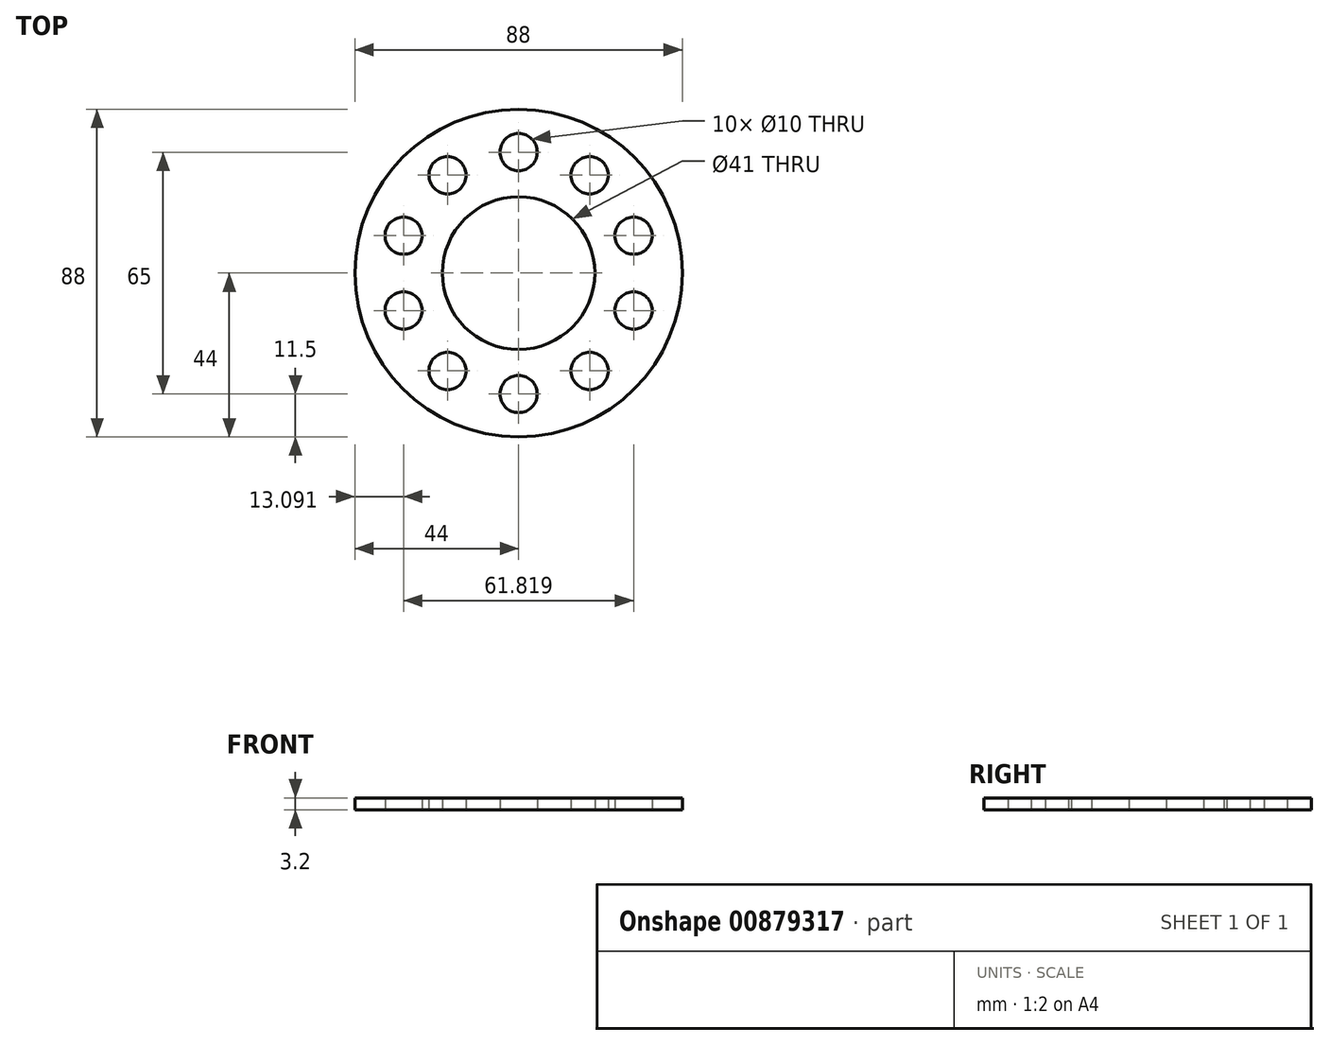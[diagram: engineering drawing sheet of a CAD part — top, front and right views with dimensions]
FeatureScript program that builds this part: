
annotation { "Feature Type Name" : "Feature", "Feature Type Description" : "" }
export const myFeature = defineFeature(function(context is Context, id is Id, definition is map)
    precondition{}
    {
        {
            var Q0;
            Q0=qCreatedBy(makeId("Top.planeOp"),FACE);
            var sketch = newSketch(context, id + "F0", { "sketchPlane" : qUnion([Q0])});
            skCircle(sketch, "E0", {"center": v(0, 0) * mm, "radius": 44 * mm});
            skCircle(sketch, "E1", {"center": v(0, 0) * mm, "radius": 20.5 * mm});
            skCircle(sketch, "E2", {"center": v(0, 32.5) * mm, "radius": 5 * mm});
            skCircle(sketch, "E3.1.0", {"center": v(-19.1, 26.3) * mm, "radius": 5 * mm});
            skCircle(sketch, "E3.2.0", {"center": v(-30.9, 10.04) * mm, "radius": 5 * mm});
            skCircle(sketch, "E3.3.0", {"center": v(-30.9, -10.04) * mm, "radius": 5 * mm});
            skCircle(sketch, "E3.4.0", {"center": v(-19.1, -26.3) * mm, "radius": 5 * mm});
            skCircle(sketch, "E3.5.0", {"center": v(0, -32.5) * mm, "radius": 5 * mm});
            skCircle(sketch, "E3.6.0", {"center": v(19.1, -26.3) * mm, "radius": 5 * mm});
            skCircle(sketch, "E3.7.0", {"center": v(30.9, -10.04) * mm, "radius": 5 * mm});
            skCircle(sketch, "E3.8.0", {"center": v(30.9, 10.04) * mm, "radius": 5 * mm});
            skCircle(sketch, "E3.9.0", {"center": v(19.1, 26.3) * mm, "radius": 5 * mm});
            skSolve(sketch);
        }
        {
            var Q0;
            Q0=makeQuery(id+"F0.imprint","IMPRINT",FACE,{"disambiguationData":[TD([[makeQuery(id+"F0.imprint","IMPRINT",EDGE,{"derivedFrom":sQuery(id+"F0.wireOp",EDGE,"E0")}),1.0]])]});
            var Q1;
            Q1=sQuery(id+"F0.wireOp",EDGE,"E0");
            extrude(context, id + "F1", {"entities" : qUnion([Q0]), "surfaceEntities" : qUnion([Q1]), "depth" : 3.2 * mm, "offsetDistance" : 25 * mm});
        }
    });
